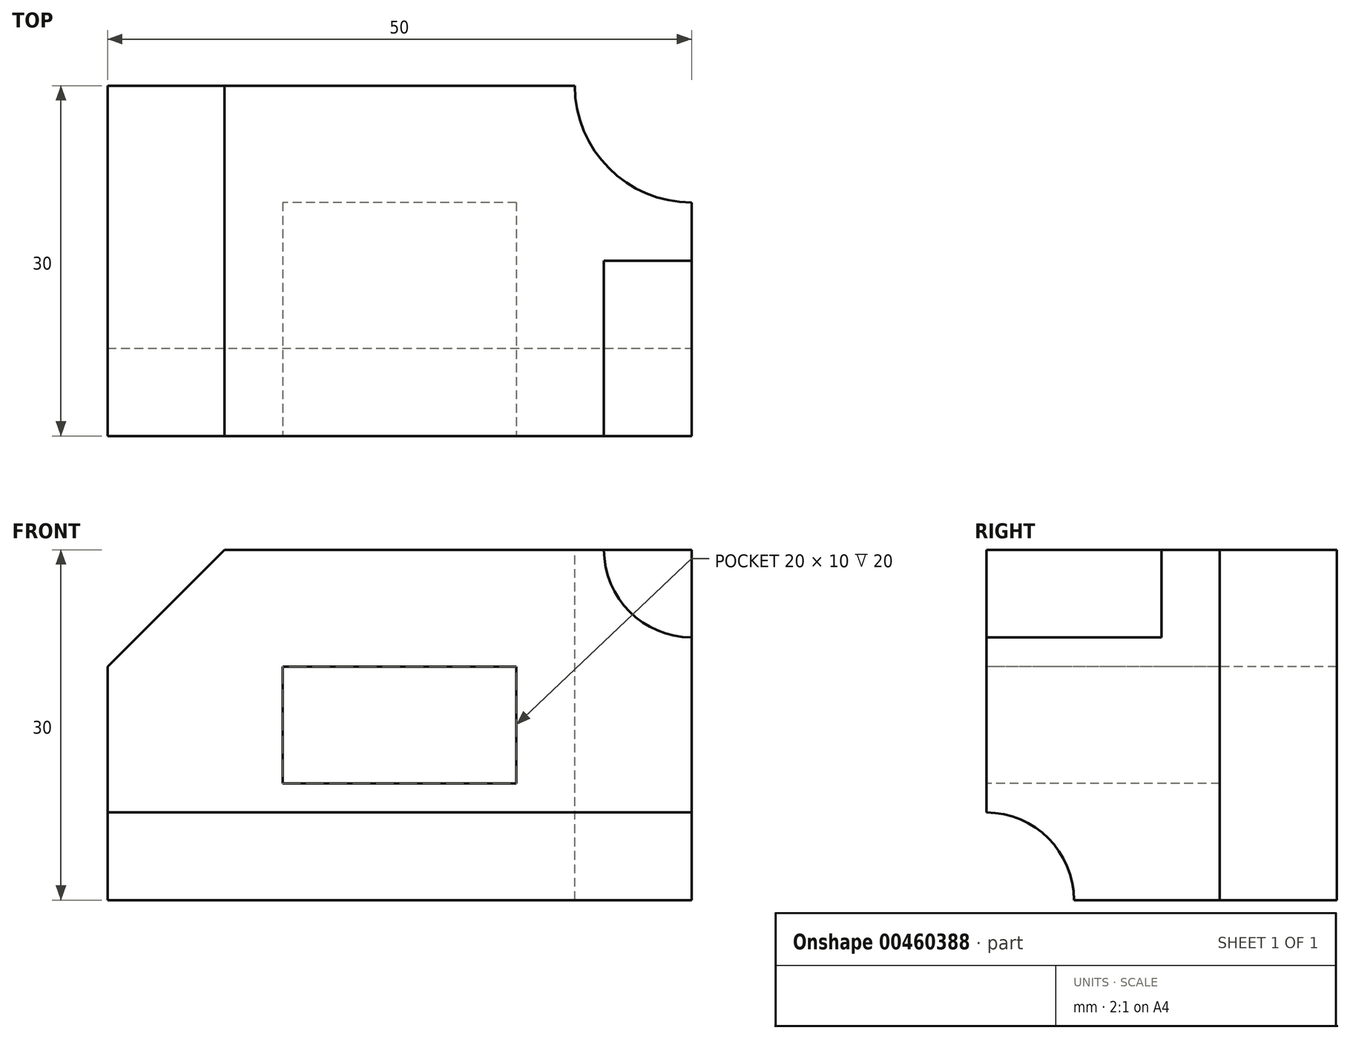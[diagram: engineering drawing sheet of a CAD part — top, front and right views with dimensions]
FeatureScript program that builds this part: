
annotation { "Feature Type Name" : "Feature", "Feature Type Description" : "" }
export const myFeature = defineFeature(function(context is Context, id is Id, definition is map)
    precondition{}
    {
        {
            var Q0;
            Q0=qCreatedBy(makeId("Front.planeOp"),FACE);
            var sketch = newSketch(context, id + "F0", { "sketchPlane" : qUnion([Q0])});
            skLineSegment(sketch, "E0.bottom", {"start": v(0, 0) * mm, "end": v(-50, 0) * mm});
            skLineSegment(sketch, "E0.top", {"start": v(0, 30) * mm, "end": v(-50, 30) * mm});
            skLineSegment(sketch, "E0.left", {"start": v(0, 0) * mm, "end": v(0, 30) * mm});
            skLineSegment(sketch, "E0.right", {"start": v(-50, 0) * mm, "end": v(-50, 30) * mm});
            skSolve(sketch);
        }
        {
            var Q0;
            Q0 = qSketchRegion(id + "F0", true);
            extrude(context, id + "F1", {"entities" : qUnion([Q0]), "depth" : 30 * mm});
        }
        {
            var Q0;
            Q0=makeQuery(id+"F1.opExtrude","CAP_FACE",FACE,{"disambiguationData":[OSD([sQuery(id+"F0.wireOp",EDGE,"E0.bottom"),sQuery(id+"F0.wireOp",EDGE,"E0.top"),sQuery(id+"F0.wireOp",EDGE,"E0.left"),sQuery(id+"F0.wireOp",EDGE,"E0.right")])],"isStart":false});
            var sketch = newSketch(context, id + "F2", { "sketchPlane" : qUnion([Q0])});
            skLineSegment(sketch, "E1", {"start": v(-50, 30) * mm, "end": v(-40, 30) * mm});
            skLineSegment(sketch, "E2", {"start": v(-50, 30) * mm, "end": v(-50, 20) * mm});
            skLineSegment(sketch, "E3", {"start": v(-50, 20) * mm, "end": v(-40, 30) * mm});
            skSolve(sketch);
        }
        {
            var Q0;
            Q0=makeQuery(id+"F2.imprint","IMPRINT",FACE,{"disambiguationData":[TD([[makeQuery(id+"F2.imprint","IMPRINT",EDGE,{"derivedFrom":sQuery(id+"F2.wireOp",EDGE,"E1")}),1.0]])]});
            extrude(context, id + "F3", {"entities" : qUnion([Q0]), "operationType" : NewBodyOperationType.REMOVE, "endBound" : BoundingType.THROUGH_ALL, "oppositeDirection" : true, "depth" : 25 * mm});
        }
        {
            var Q0;
            Q0=makeQuery(id+"F1.opExtrude","CAP_FACE",FACE,{"disambiguationData":[OSD([sQuery(id+"F0.wireOp",EDGE,"E0.bottom"),sQuery(id+"F0.wireOp",EDGE,"E0.top"),sQuery(id+"F0.wireOp",EDGE,"E0.left"),sQuery(id+"F0.wireOp",EDGE,"E0.right")])],"isStart":false});
            var sketch = newSketch(context, id + "F4", { "sketchPlane" : qUnion([Q0])});
            skLineSegment(sketch, "E4", {"start": v(-50, 20) * mm, "end": v(-50, 10) * mm});
            skLineSegment(sketch, "E5", {"start": v(-50, 10) * mm, "end": v(-35, 10) * mm});
            skLineSegment(sketch, "E6", {"start": v(-35, 10) * mm, "end": v(-15, 10) * mm});
            skLineSegment(sketch, "E7", {"start": v(-15, 10) * mm, "end": v(-15, 20) * mm});
            skLineSegment(sketch, "E8", {"start": v(-15, 20) * mm, "end": v(-35, 20) * mm});
            skLineSegment(sketch, "E9", {"start": v(-35, 20) * mm, "end": v(-50, 20) * mm});
            skLineSegment(sketch, "E10", {"start": v(-35, 20) * mm, "end": v(-35, 10) * mm});
            skSolve(sketch);
        }
        {
            var Q0;
            Q0=makeQuery(id+"F4.imprint","IMPRINT",FACE,{"disambiguationData":[TD([[makeQuery(id+"F4.imprint","IMPRINT",EDGE,{"derivedFrom":sQuery(id+"F4.wireOp",EDGE,"E6")}),1.0]])]});
            extrude(context, id + "F5", {"entities" : qUnion([Q0]), "operationType" : NewBodyOperationType.REMOVE, "oppositeDirection" : true, "depth" : 20 * mm});
        }
        {
            var Q0;
            Q0=makeQuery(id+"F1.opExtrude","SWEPT_FACE",FACE,{"disambiguationData":[OSD([sQuery(id+"F0.wireOp",EDGE,"E0.top")])]});
            var sketch = newSketch(context, id + "F6", { "sketchPlane" : qUnion([Q0])});
            skCircle(sketch, "E11", {"center": v(0, 0) * mm, "radius": 10 * mm});
            skSolve(sketch);
        }
        {
            var Q0;
            {var subQ0=sQuery(id+"F6.wireOp",EDGE,"E11");var subQ1=sQuery(id+"F0.wireOp",EDGE,"E0.top");var subQ4=makeQuery(id+"F1.opExtrude","CAP_EDGE",EDGE,{"disambiguationData":[OSD([subQ1])],"isStart":true});var subQ5=makeQuery(id+"F6.imprint","INTERSECT",VERTEX,{"derivedFrom":[subQ4,subQ0]});Q0=makeQuery(id+"F6.imprint","IMPRINT",FACE,{"disambiguationData":[TD([[makeQuery(id+"F6.imprint","IMPRINT",EDGE,{"disambiguationData":[TD([[subQ5,-1.0]])],"derivedFrom":subQ0}),1.0]])]});}
            extrude(context, id + "F7", {"entities" : qUnion([Q0]), "operationType" : NewBodyOperationType.REMOVE, "endBound" : BoundingType.THROUGH_ALL, "oppositeDirection" : true, "depth" : 25 * mm});
        }
        {
            var Q0;
            Q0=makeQuery(id+"F1.opExtrude","SWEPT_FACE",FACE,{"disambiguationData":[OSD([sQuery(id+"F0.wireOp",EDGE,"E0.left")])]});
            var sketch = newSketch(context, id + "F8", { "sketchPlane" : qUnion([Q0])});
            skCircle(sketch, "E12", {"center": v(-30, 0) * mm, "radius": 7.5 * mm});
            skSolve(sketch);
        }
        {
            var Q0;
            {var subQ0=sQuery(id+"F8.wireOp",EDGE,"E12");var subQ1=sQuery(id+"F0.wireOp",EDGE,"E0.left");var subQ2=makeQuery(id+"F1.opExtrude","CAP_EDGE",EDGE,{"disambiguationData":[OSD([subQ1])],"isStart":false});var subQ3=makeQuery(id+"F8.imprint","INTERSECT",VERTEX,{"derivedFrom":[subQ2,subQ0]});Q0=makeQuery(id+"F8.imprint","IMPRINT",FACE,{"disambiguationData":[TD([[makeQuery(id+"F8.imprint","IMPRINT",EDGE,{"disambiguationData":[TD([[subQ3,1.0]])],"derivedFrom":subQ0}),1.0]])]});}
            extrude(context, id + "F9", {"entities" : qUnion([Q0]), "operationType" : NewBodyOperationType.REMOVE, "endBound" : BoundingType.THROUGH_ALL, "oppositeDirection" : true, "depth" : 25 * mm});
        }
        {
            var Q0;
            Q0=makeQuery(id+"F1.opExtrude","CAP_FACE",FACE,{"disambiguationData":[OSD([sQuery(id+"F0.wireOp",EDGE,"E0.bottom"),sQuery(id+"F0.wireOp",EDGE,"E0.top"),sQuery(id+"F0.wireOp",EDGE,"E0.left"),sQuery(id+"F0.wireOp",EDGE,"E0.right")])],"isStart":false});
            var sketch = newSketch(context, id + "F10", { "sketchPlane" : qUnion([Q0])});
            skCircle(sketch, "E13", {"center": v(0, 30) * mm, "radius": 7.5 * mm});
            skSolve(sketch);
        }
        {
            var Q0;
            {var subQ0=sQuery(id+"F10.wireOp",EDGE,"E13");var subQ1=makeQuery(id+"F1.opExtrude","CAP_EDGE",EDGE,{"disambiguationData":[OSD([sQuery(id+"F0.wireOp",EDGE,"E0.top")])],"isStart":false});var subQ2=makeQuery(id+"F10.imprint","INTERSECT",VERTEX,{"derivedFrom":[subQ1,subQ0]});Q0=makeQuery(id+"F10.imprint","IMPRINT",FACE,{"disambiguationData":[TD([[makeQuery(id+"F10.imprint","IMPRINT",EDGE,{"disambiguationData":[TD([[subQ2,-1.0]])],"derivedFrom":subQ0}),1.0]])]});}
            extrude(context, id + "F11", {"entities" : qUnion([Q0]), "operationType" : NewBodyOperationType.REMOVE, "oppositeDirection" : true, "depth" : 15 * mm});
        }
    });
